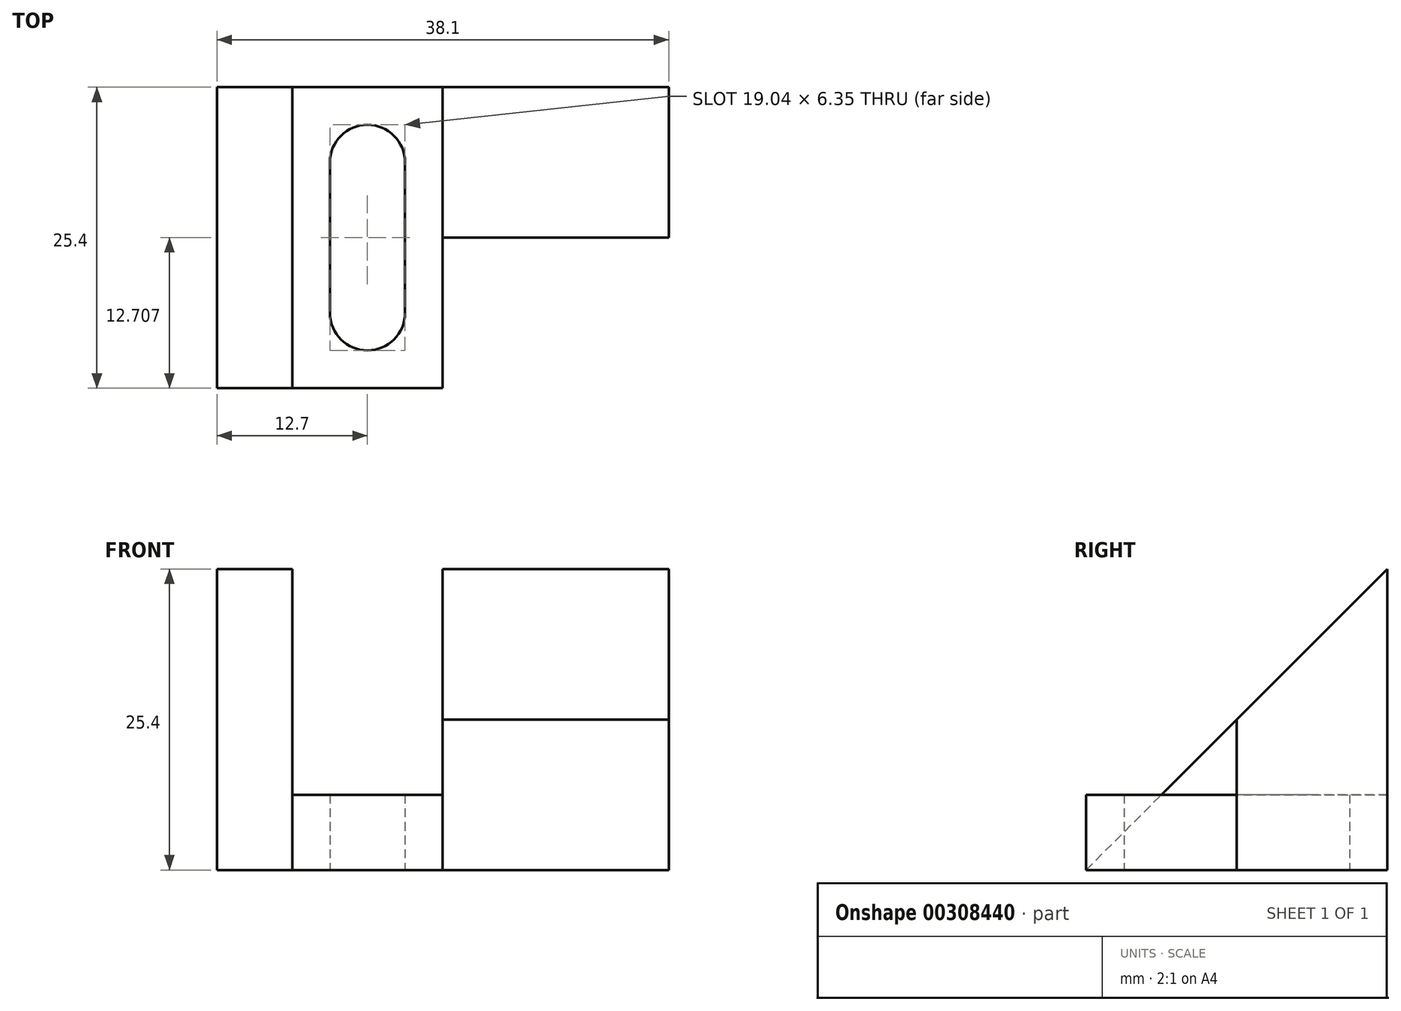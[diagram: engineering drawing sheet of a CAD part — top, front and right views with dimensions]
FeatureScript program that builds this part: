
annotation { "Feature Type Name" : "Feature", "Feature Type Description" : "" }
export const myFeature = defineFeature(function(context is Context, id is Id, definition is map)
    precondition{}
    {
        {
            var Q0;
            Q0=qCreatedBy(makeId("Top.planeOp"),FACE);
            var sketch = newSketch(context, id + "F0", { "sketchPlane" : qUnion([Q0])});
            skLineSegment(sketch, "E0", {"start": v(0, 0) * mm, "end": v(0, 25.4) * mm});
            skLineSegment(sketch, "E1", {"start": v(0, 25.4) * mm, "end": v(38.1, 25.4) * mm});
            skLineSegment(sketch, "E2", {"start": v(38.1, 25.4) * mm, "end": v(38.1, 12.7) * mm});
            skLineSegment(sketch, "E3", {"start": v(38.1, 12.7) * mm, "end": v(19.05, 12.7) * mm});
            skLineSegment(sketch, "E4", {"start": v(19.05, 12.7) * mm, "end": v(19.05, 0) * mm});
            skLineSegment(sketch, "E5", {"start": v(19.05, 0) * mm, "end": v(0, 0) * mm});
            skLineSegment(sketch, "E6", {"start": v(6.35, 25.4) * mm, "end": v(6.35, 0) * mm});
            skLineSegment(sketch, "E7", {"start": v(6.35, 25.4) * mm, "end": v(19.05, 25.4) * mm});
            skLineSegment(sketch, "E8", {"start": v(19.05, 25.4) * mm, "end": v(19.05, 12.7) * mm});
            skLineSegment(sketch, "E9.bottom", {"start": v(9.53, 19.05) * mm, "end": v(15.88, 19.05) * mm});
            skLineSegment(sketch, "E9.top", {"start": v(9.53, 6.35) * mm, "end": v(15.88, 6.35) * mm});
            skLineSegment(sketch, "E9.left", {"start": v(9.53, 19.05) * mm, "end": v(9.53, 6.35) * mm});
            skLineSegment(sketch, "E9.right", {"start": v(15.88, 19.05) * mm, "end": v(15.88, 6.35) * mm});
            skArc(sketch, "E10", {"start": v(15.88, 19.05) * mm, "mid": v(12.7, 22.23) * mm, "end": v(9.53, 19.05) * mm});
            skArc(sketch, "E11", {"start": v(9.53, 6.35) * mm, "mid": v(12.7, 3.17) * mm, "end": v(15.88, 6.35) * mm});
            skSolve(sketch);
        }
        {
            var Q0;
            Q0 = qSketchRegion(id + "F0", true);
            extrude(context, id + "F1", {"entities" : qUnion([Q0]), "depth" : 25.4 * mm});
        }
        {
            var Q0;
            Q0=makeQuery(id+"F1.opExtrude","CAP_FACE",FACE,{"disambiguationData":[OSD([sQuery(id+"F0.wireOp",EDGE,"E0"),sQuery(id+"F0.wireOp",EDGE,"E1"),sQuery(id+"F0.wireOp",EDGE,"E2"),sQuery(id+"F0.wireOp",EDGE,"E3"),sQuery(id+"F0.wireOp",EDGE,"E4"),sQuery(id+"F0.wireOp",EDGE,"E5"),sQuery(id+"F0.wireOp",EDGE,"E7"),sQuery(id+"F0.wireOp",EDGE,"E9.left"),sQuery(id+"F0.wireOp",EDGE,"E9.right"),sQuery(id+"F0.wireOp",EDGE,"E10"),sQuery(id+"F0.wireOp",EDGE,"E11")])],"isStart":false});
            var sketch = newSketch(context, id + "F2", { "sketchPlane" : qUnion([Q0])});
            skLineSegment(sketch, "E12", {"start": v(6.35, 0) * mm, "end": v(6.35, 25.4) * mm});
            skLineSegment(sketch, "E13", {"start": v(6.35, 25.4) * mm, "end": v(19.05, 25.4) * mm});
            skLineSegment(sketch, "E14", {"start": v(19.05, 25.4) * mm, "end": v(19.05, 0) * mm});
            skLineSegment(sketch, "E15", {"start": v(19.05, 0) * mm, "end": v(6.35, 0) * mm});
            skLineSegment(sketch, "E16", {"start": v(9.53, 19.05) * mm, "end": v(9.53, 6.35) * mm});
            skLineSegment(sketch, "E17", {"start": v(15.88, 19.05) * mm, "end": v(15.88, 6.35) * mm});
            skArc(sketch, "E18", {"start": v(15.88, 19.05) * mm, "mid": v(12.7, 22.23) * mm, "end": v(9.53, 19.05) * mm});
            skArc(sketch, "E19", {"start": v(9.53, 6.35) * mm, "mid": v(12.7, 3.18) * mm, "end": v(15.88, 6.35) * mm});
            skSolve(sketch);
        }
        {
            var Q0;
            Q0 = qSketchRegion(id + "F2", true);
            extrude(context, id + "F3", {"entities" : qUnion([Q0]), "operationType" : NewBodyOperationType.REMOVE, "oppositeDirection" : true, "depth" : 19.05 * mm});
        }
        {
            var Q0;
            Q0=makeQuery(id+"F1.opExtrude","SWEPT_FACE",FACE,{"disambiguationData":[OSD([sQuery(id+"F0.wireOp",EDGE,"E2")])]});
            var sketch = newSketch(context, id + "F4", { "sketchPlane" : qUnion([Q0])});
            skLineSegment(sketch, "E20", {"start": v(25.4, 25.4) * mm, "end": v(0, 0) * mm});
            skLineSegment(sketch, "E21", {"start": v(0, 0) * mm, "end": v(0, 25.4) * mm});
            skLineSegment(sketch, "E22", {"start": v(0, 25.4) * mm, "end": v(25.4, 25.4) * mm});
            skSolve(sketch);
        }
        {
            var Q0;
            Q0 = qSketchRegion(id + "F4", true);
            extrude(context, id + "F5", {"entities" : qUnion([Q0]), "operationType" : NewBodyOperationType.REMOVE, "endBound" : BoundingType.THROUGH_ALL, "oppositeDirection" : true, "depth" : 25.4 * mm});
        }
        {
            var Q0;
            Q0=qCreatedBy(makeId("Top.planeOp"),FACE);
            var sketch = newSketch(context, id + "F6", { "sketchPlane" : qUnion([Q0])});
            skLineSegment(sketch, "E23", {"start": v(6.35, 6.35) * mm, "end": v(6.35, 0) * mm});
            skLineSegment(sketch, "E24", {"start": v(6.35, 0) * mm, "end": v(19.05, 0) * mm});
            skLineSegment(sketch, "E25", {"start": v(19.05, 0) * mm, "end": v(19.05, 6.35) * mm});
            skLineSegment(sketch, "E26", {"start": v(6.35, 6.35) * mm, "end": v(9.52, 6.35) * mm});
            skLineSegment(sketch, "E27", {"start": v(19.05, 6.35) * mm, "end": v(15.87, 6.35) * mm});
            skArc(sketch, "E28", {"start": v(9.52, 6.35) * mm, "mid": v(12.7, 3.19) * mm, "end": v(15.87, 6.35) * mm});
            skSolve(sketch);
        }
        {
            var Q0;
            Q0 = qSketchRegion(id + "F6", true);
            extrude(context, id + "F7", {"entities" : qUnion([Q0]), "operationType" : NewBodyOperationType.ADD, "depth" : 6.35 * mm});
        }
    });
